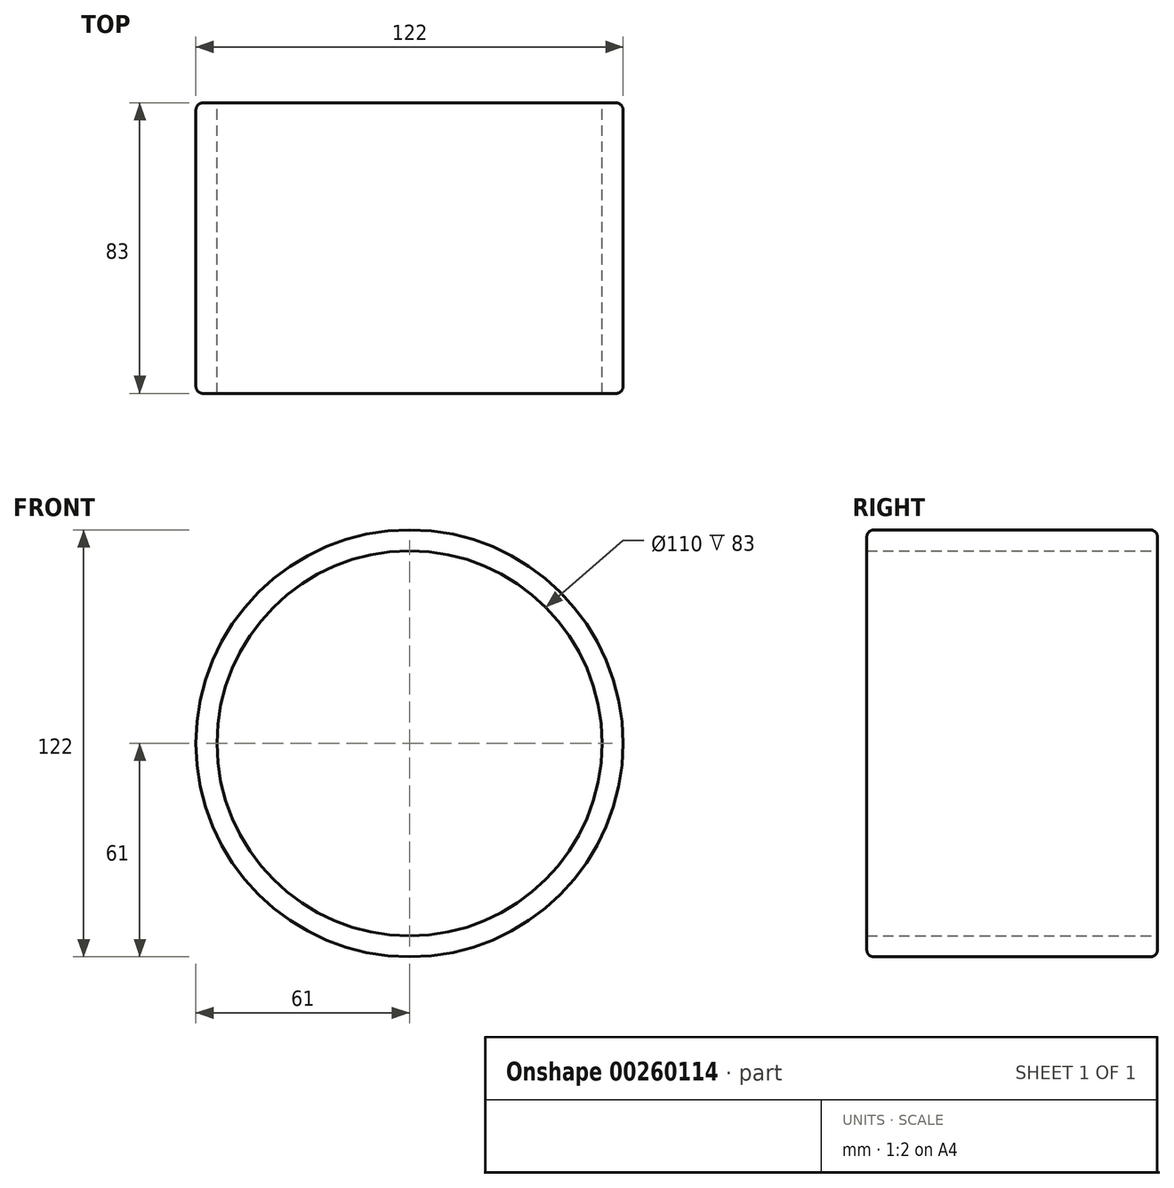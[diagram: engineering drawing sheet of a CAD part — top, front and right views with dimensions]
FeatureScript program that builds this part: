
annotation { "Feature Type Name" : "Feature", "Feature Type Description" : "" }
export const myFeature = defineFeature(function(context is Context, id is Id, definition is map)
    precondition{}
    {
        {
            var Q0;
            Q0=qCreatedBy(makeId("Front.planeOp"),FACE);
            var sketch = newSketch(context, id + "F0", { "sketchPlane" : qUnion([Q0])});
            skCircle(sketch, "E0", {"center": v(0, 0) * mm, "radius": 61 * mm});
            skCircle(sketch, "E1", {"center": v(0, 0) * mm, "radius": 55 * mm});
            skSolve(sketch);
        }
        {
            var Q0;
            Q0=makeQuery(id+"F0.imprint","IMPRINT",FACE,{"disambiguationData":[TD([[makeQuery(id+"F0.imprint","IMPRINT",EDGE,{"derivedFrom":sQuery(id+"F0.wireOp",EDGE,"E0")}),1.0]])]});
            extrude(context, id + "F1", {"entities" : qUnion([Q0]), "endBound" : BoundingType.SYMMETRIC, "depth" : 83 * mm});
        }
        {
            var Q0;
            Q0=makeQuery(id+"F1.opExtrude","CAP_EDGE",EDGE,{"disambiguationData":[OSD([sQuery(id+"F0.wireOp",EDGE,"E0")])],"isStart":false});
            var Q1;
            Q1=makeQuery(id+"F1.opExtrude","CAP_EDGE",EDGE,{"disambiguationData":[OSD([sQuery(id+"F0.wireOp",EDGE,"E0")])],"isStart":true});
            fillet(context, id + "F2", {"entities" : qUnion([Q0, Q1]), "radius" : 2 * mm, "tangentPropagation" : true, "allowEdgeOverflow" : false});
        }
    });
